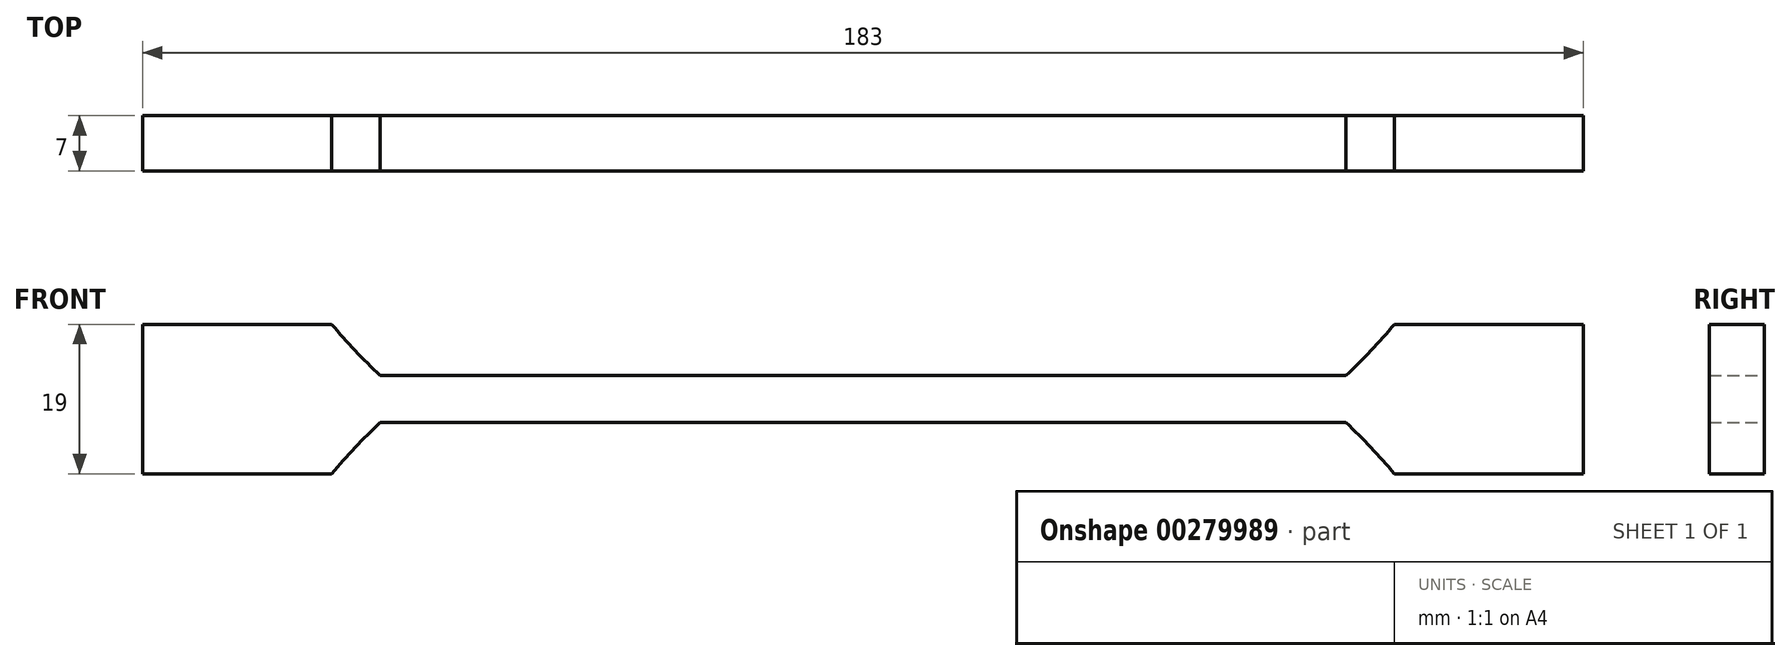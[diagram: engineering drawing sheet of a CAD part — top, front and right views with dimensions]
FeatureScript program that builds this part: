
annotation { "Feature Type Name" : "Feature", "Feature Type Description" : "" }
export const myFeature = defineFeature(function(context is Context, id is Id, definition is map)
    precondition{}
    {
        {
            var Q0;
            Q0=qCreatedBy(makeId("Front.planeOp"),FACE);
            var sketch = newSketch(context, id + "F0", { "sketchPlane" : qUnion([Q0])});
            skLineSegment(sketch, "E0", {"start": v(0, 3) * mm, "end": v(61.35, 3) * mm});
            skArc(sketch, "E1", {"start": v(61.35, 3) * mm, "mid": v(64.52, 6.16) * mm, "end": v(67.5, 9.5) * mm});
            skLineSegment(sketch, "E2", {"start": v(67.5, 9.5) * mm, "end": v(91.5, 9.5) * mm});
            skLineSegment(sketch, "E3", {"start": v(91.5, 9.5) * mm, "end": v(91.5, 0) * mm});
            skArc(sketch, "E4.MirrorCS", {"start": v(61.35, -3) * mm, "mid": v(64.52, -6.16) * mm, "end": v(67.5, -9.5) * mm});
            skLineSegment(sketch, "E5.MirrorCS", {"start": v(91.5, -9.5) * mm, "end": v(91.5, 0) * mm});
            skLineSegment(sketch, "E6.MirrorCS", {"start": v(0, -3) * mm, "end": v(61.35, -3) * mm});
            skLineSegment(sketch, "E7.MirrorCS", {"start": v(67.5, -9.5) * mm, "end": v(91.5, -9.5) * mm});
            skArc(sketch, "E8.MirrorCS", {"start": v(-61.35, 3) * mm, "mid": v(-64.52, 6.16) * mm, "end": v(-67.5, 9.5) * mm});
            skArc(sketch, "E9.MirrorCS", {"start": v(-61.35, -3) * mm, "mid": v(-64.52, -6.16) * mm, "end": v(-67.5, -9.5) * mm});
            skLineSegment(sketch, "E10.MirrorCS", {"start": v(-67.5, -9.5) * mm, "end": v(-91.5, -9.5) * mm});
            skLineSegment(sketch, "E11.MirrorCS", {"start": v(0, -3) * mm, "end": v(-61.35, -3) * mm});
            skLineSegment(sketch, "E12.MirrorCS", {"start": v(0, 3) * mm, "end": v(-61.35, 3) * mm});
            skLineSegment(sketch, "E13.MirrorCS", {"start": v(-67.5, 9.5) * mm, "end": v(-91.5, 9.5) * mm});
            skLineSegment(sketch, "E14.MirrorCS", {"start": v(-91.5, -9.5) * mm, "end": v(-91.5, 0) * mm});
            skLineSegment(sketch, "E15.MirrorCS", {"start": v(-91.5, 9.5) * mm, "end": v(-91.5, 0) * mm});
            skSolve(sketch);
        }
        {
            var Q0;
            Q0=makeQuery(id+"F0.imprint","IMPRINT",FACE,{"disambiguationData":[TD([[makeQuery(id+"F0.imprint","IMPRINT",EDGE,{"derivedFrom":sQuery(id+"F0.wireOp",EDGE,"E0")}),-1.0]])]});
            extrude(context, id + "F1", {"entities" : qUnion([Q0]), "endBound" : BoundingType.SYMMETRIC, "depth" : 7 * mm});
        }
    });
